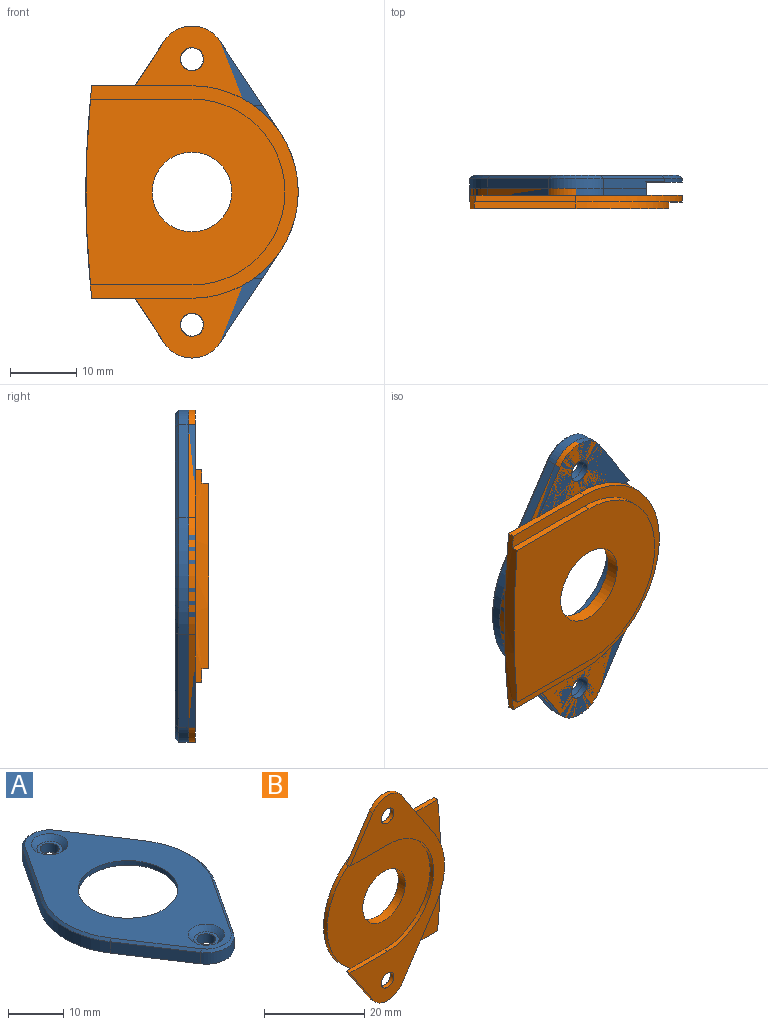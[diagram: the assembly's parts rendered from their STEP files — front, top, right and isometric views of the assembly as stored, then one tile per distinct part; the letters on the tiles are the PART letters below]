
ASSEMBLY  parts=2 mates=1
PART A: 30 faces, bbox 32x50x3 mm
  f0: plane 13.95x9.19mm, normal (0.84,0.55,0), area 31.7mm2, adj f8,f12,f14,f20,f26,f29
  f1: cone r=4.75mm half-angle=45deg, axis (0,0,-1), area 6.6mm2, adj f2,f8,f12,f13
  f2: plane 14.23x9.6mm, normal (-0.59,0.39,0.71), area 11.8mm2, adj f1,f3,f11,f13
  f3: cone r=15.75mm half-angle=45deg, axis (0,0,-1), area 13mm2, adj f2,f4,f10,f13
  f4: plane 14.23x9.6mm, normal (-0.59,-0.39,0.71), area 11.8mm2, adj f3,f5,f9,f13
  f5: cone r=4.75mm half-angle=45deg, axis (0,0,-1), area 6.6mm2, adj f4,f6,f13,f22
  f6: plane 14.23x9.6mm, normal (0.59,-0.39,0.71), area 11.8mm2, adj f5,f7,f13,f21
  f7: cone r=15.75mm half-angle=45deg, axis (0,0,-1), area 13mm2, adj f6,f8,f13,f20
  f8: plane 14.23x9.6mm, normal (0.59,0.39,0.71), area 11.8mm2, adj f0,f1,f7,f13
  f9: plane 13.95x9.19mm, normal (-0.84,-0.55,0), area 41.8mm2, adj f4,f10,f22,f29
  f10: cylinder r=16mm len=17.6mm, axis (0,0,1), area 46.6mm2, adj f3,f9,f11,f29
  f11: plane 13.95x9.19mm, normal (-0.84,0.55,0), area 41.8mm2, adj f2,f10,f12,f29
  f12: cylinder r=5mm len=8.35mm, axis (0,0,1), area 24.7mm2, adj f0,f1,f11,f29
  f13: plane 49x31mm, normal (0,0,1), area 665.1mm2, adj f1,f2,f3,f4,f5,f6,f7,f8
  f14: plane 28.95x26mm, normal (0,0,-1), area 377mm2, adj f0,f15,f20,f21,f23,f24,f25,f26
  f15: cylinder r=9mm len=18mm, axis (0,0,1), area 56.5mm2, adj f13,f14
  f16: cone r=2.5mm half-angle=45deg, axis (0,0,1), area 24.9mm2, adj f13,f28
  f17: cylinder r=1.7mm len=3.4mm, axis (0,0,1), area 21.4mm2, adj f28,f29
  f18: cone r=2.5mm half-angle=45deg, axis (0,0,1), area 24.9mm2, adj f13,f27
  f19: cylinder r=1.7mm len=3.4mm, axis (0,0,1), area 21.4mm2, adj f27,f29
  f20: cylinder r=16mm len=17.6mm, axis (0,0,1), area 9.3mm2, adj f0,f7,f14,f21
  f21: plane 13.95x9.19mm, normal (0.84,-0.55,0), area 31.7mm2, adj f6,f14,f20,f22,f23,f29
  f22: cylinder r=5mm len=8.35mm, axis (0,0,1), area 24.7mm2, adj f5,f9,f21,f29
  f23: plane 10.89x2mm, normal (0,1,0), area 21.8mm2, adj f14,f21,f24,f29
  f24: cylinder r=13mm len=25.98mm, axis (0,0,-1), area 79.9mm2, adj f14,f23,f25,f29
  f25: plane 2x0.02mm, normal (1,0,0), area 0mm2, adj f14,f24,f26,f29
  f26: plane 11.1x2mm, normal (0,-1,0), area 22.2mm2, adj f0,f14,f25,f29
  f27: plane 4.6x4.6mm, normal (0,0,1), area 7.5mm2, adj f18,f19
  f28: plane 4.6x4.6mm, normal (0,0,1), area 7.5mm2, adj f16,f17
  f29: plane 50x26.6mm, normal (0,0,-1), area 399.5mm2, adj f0,f9,f10,f11,f12,f17,f19,f21
PART B: 28 faces, bbox 32x3x50 mm
  f0: plane 9.75x6.42mm, normal (-0.84,0,0.55), area 11.7mm2, adj f2,f7,f9,f27
  f1: plane 19.22x12mm, normal (0,1,0), area 99.8mm2, adj f6,f8,f12,f13,f21,f22,f26
  f2: plane 50x26.6mm, normal (0,-1,0), area 397.5mm2, adj f0,f3,f5,f6,f8,f9,f10,f11
  f3: cylinder r=13mm len=26mm, axis (0,-1,0), area 40.8mm2, adj f2,f25,f26,f27
  f4: cylinder r=6mm len=12mm, axis (0,-1,0), area 75.4mm2, adj f19,f25
  f5: cylinder r=1.75mm len=3.5mm, axis (0,-1,0), area 11mm2, adj f2,f7
  f6: cylinder r=1.75mm len=3.5mm, axis (0,-1,0), area 11mm2, adj f1,f2
  f7: plane 19.22x12mm, normal (0,1,0), area 99.8mm2, adj f0,f5,f9,f10,f20,f21,f27
  f8: plane 9.75x6.42mm, normal (-0.84,0,-0.55), area 11.7mm2, adj f1,f2,f13,f26
  f9: cylinder r=5mm len=8.35mm, axis (0,-1,0), area 9.9mm2, adj f0,f2,f7,f10
  f10: plane 13.95x9.19mm, normal (0.84,0,0.55), area 16.7mm2, adj f2,f7,f9,f11,f14
  f11: cylinder r=16mm len=17.6mm, axis (0,-1,0), area 18.6mm2, adj f2,f10,f12,f14,f24
  f12: plane 13.95x9.19mm, normal (0.84,0,-0.55), area 16.7mm2, adj f1,f2,f11,f13,f24
  f13: cylinder r=5mm len=8.35mm, axis (0,-1,0), area 9.9mm2, adj f1,f2,f8,f12
  f14: plane 16x7.38mm, normal (0,-1,0), area 38.6mm2, adj f10,f11,f20,f23
  f15: plane 15.3x1mm, normal (0,0,1), area 15.3mm2, adj f16,f18,f19,f23
  f16: cylinder r=14mm len=28mm, axis (0,-1,0), area 44mm2, adj f15,f17,f18,f19
  f17: plane 15.3x1mm, normal (0,0,-1), area 15.3mm2, adj f16,f18,f19,f23
  f18: plane 32x31.3mm, normal (0,1,0), area 155mm2, adj f15,f16,f17,f20,f21,f22,f23
  f19: plane 30x28mm, normal (0,1,0), area 636.2mm2, adj f4,f15,f16,f17,f23
  f20: plane 15.08x1mm, normal (0,0,1), area 15.1mm2, adj f7,f14,f18,f21,f23
  f21: cylinder r=16mm len=32mm, axis (0,1,0), area 50.3mm2, adj f1,f7,f18,f20,f22,f25
  f22: plane 15.08x1mm, normal (0,0,-1), area 15.1mm2, adj f1,f18,f21,f23,f24
  f23: cylinder r=140mm len=32mm, axis (0,1,0), area 60.1mm2, adj f14,f15,f17,f18,f19,f20,f22,f24
  f24: plane 16x7.38mm, normal (0,-1,0), area 38.6mm2, adj f11,f12,f22,f23
  f25: plane 28.99x26mm, normal (0,-1,0), area 516mm2, adj f3,f4,f21,f26,f27
  f26: plane 10.58x1mm, normal (0,0,1), area 10.6mm2, adj f1,f2,f3,f8,f25
  f27: plane 10.58x1mm, normal (0,0,-1), area 10.6mm2, adj f0,f2,f3,f7,f25
PLACE A rot(axis=(-1,0,0),90deg) t=(2.2,-3,0)mm
PLACE B rot(axis=(0,0,1),180deg) t=(-22.8,-4,0)mm
MATE cylindrical B.f5 <-> A.f5  axis (0,-1,0) through (-10.3,-4,20)mm
